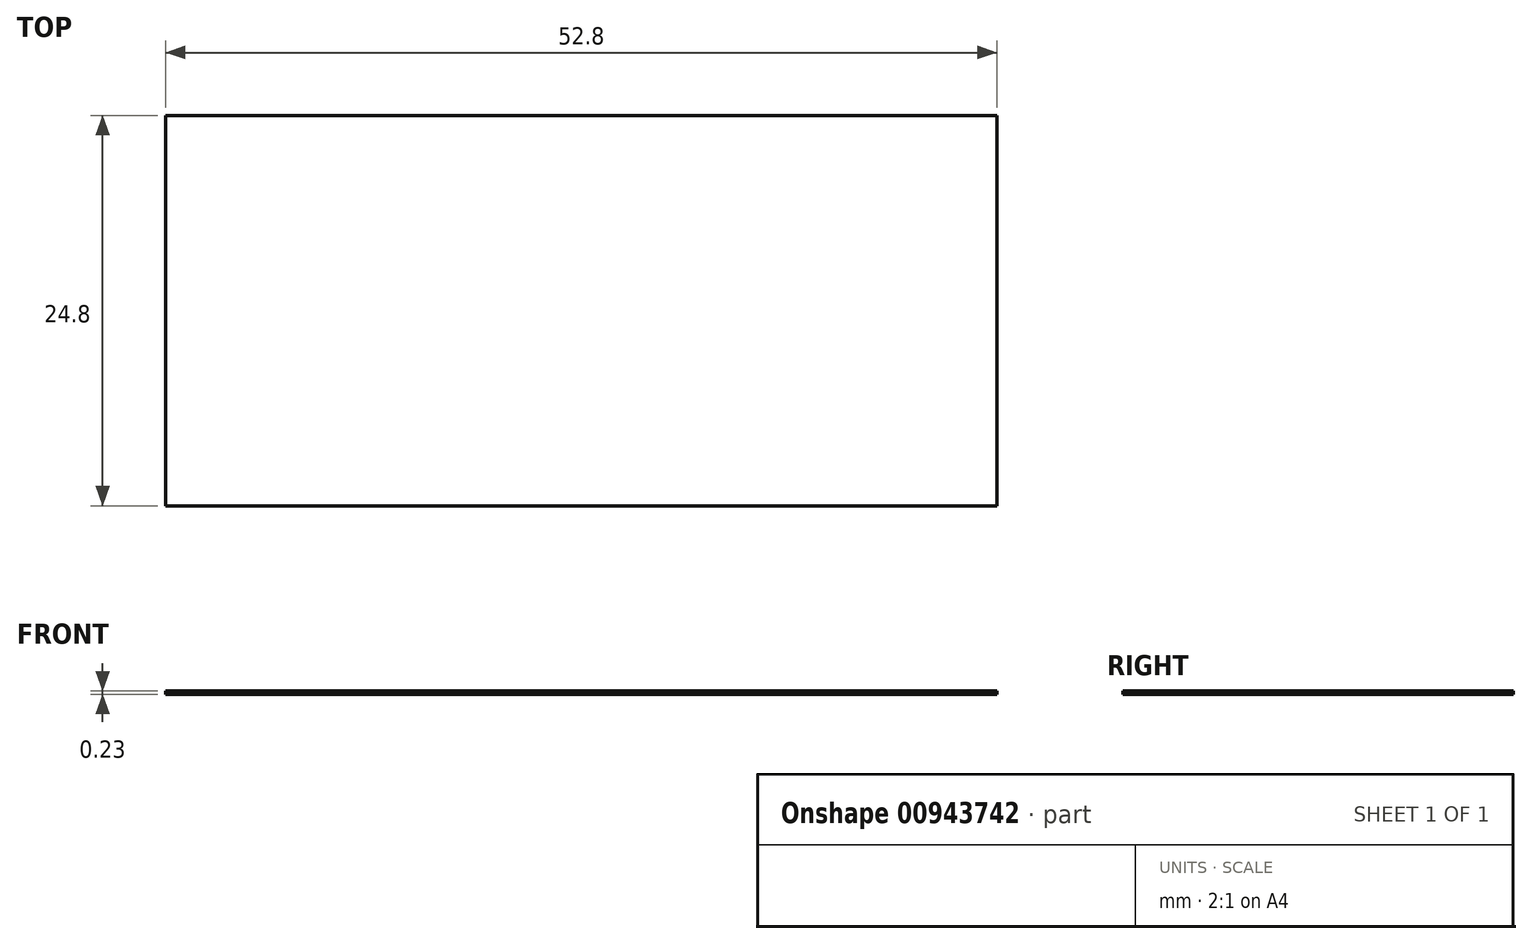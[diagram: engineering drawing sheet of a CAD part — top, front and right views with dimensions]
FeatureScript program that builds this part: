
annotation { "Feature Type Name" : "Feature", "Feature Type Description" : "" }
export const myFeature = defineFeature(function(context is Context, id is Id, definition is map)
    precondition{}
    {
        {
            var Q0;
            Q0=qCreatedBy(makeId("Top.planeOp"),FACE);
            var sketch = newSketch(context, id + "F0", { "sketchPlane" : qUnion([Q0])});
            skLineSegment(sketch, "E0.bottom", {"start": v(0, 0) * mm, "end": v(-52.8, 0) * mm});
            skLineSegment(sketch, "E0.top", {"start": v(0, 24.8) * mm, "end": v(-52.8, 24.8) * mm});
            skLineSegment(sketch, "E0.left", {"start": v(0, 0) * mm, "end": v(0, 24.8) * mm});
            skLineSegment(sketch, "E0.right", {"start": v(-52.8, 0) * mm, "end": v(-52.8, 24.8) * mm});
            skSolve(sketch);
        }
        {
            var Q0;
            Q0 = qSketchRegion(id + "F0", true);
            extrude(context, id + "F1", {"entities" : qUnion([Q0]), "depth" : 0.23 * mm, "offsetDistance" : 25 * mm});
        }
    });
